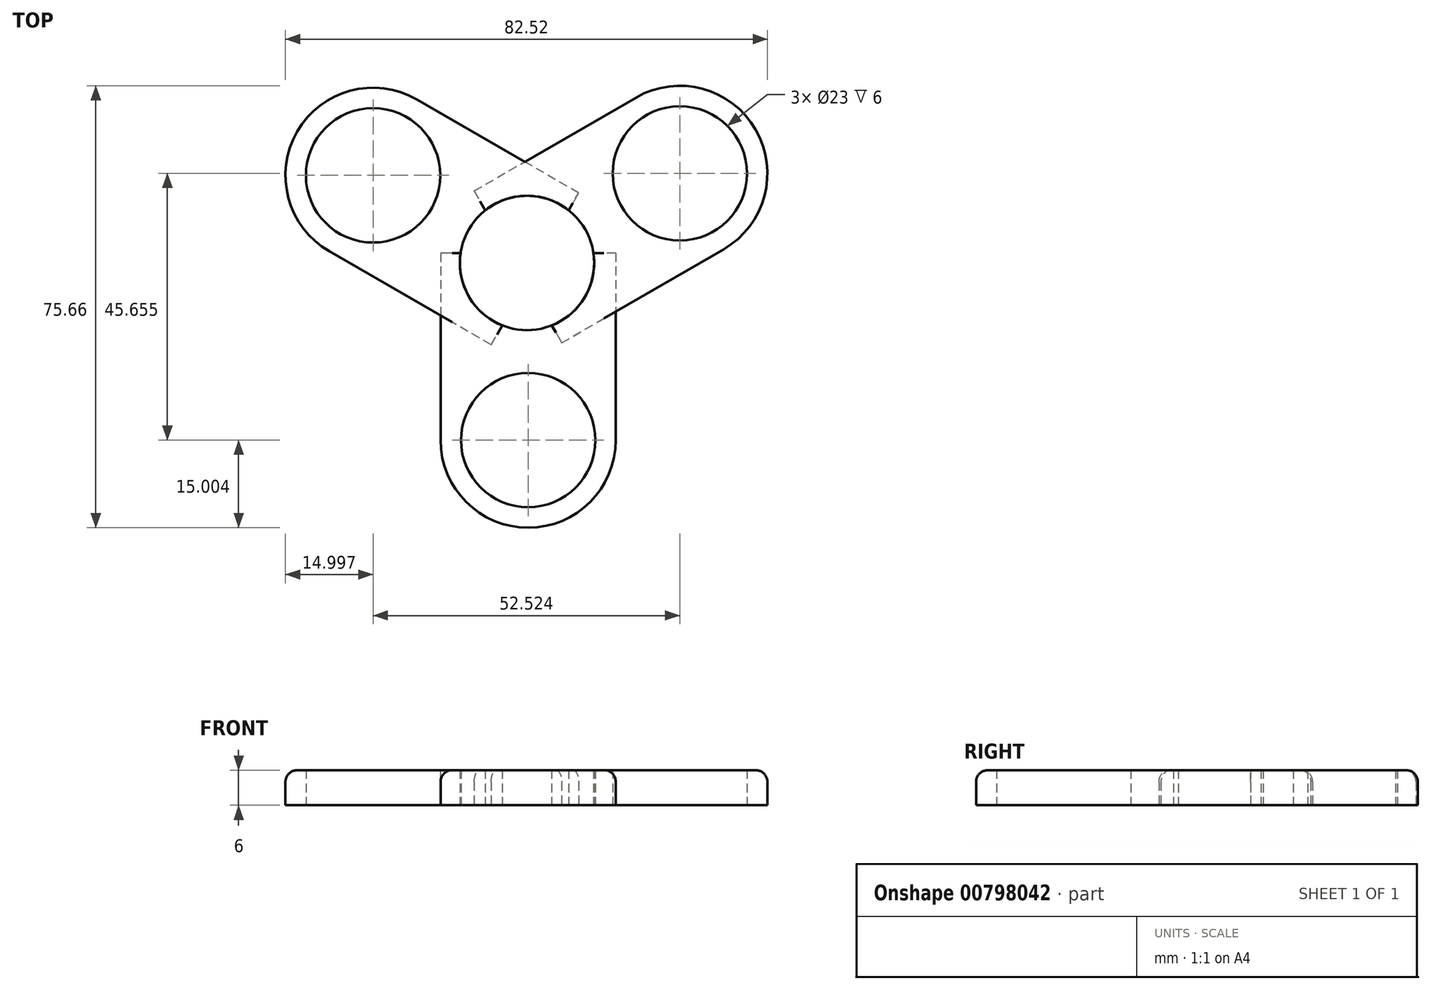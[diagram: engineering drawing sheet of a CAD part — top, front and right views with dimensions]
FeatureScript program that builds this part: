
annotation { "Feature Type Name" : "Feature", "Feature Type Description" : "" }
export const myFeature = defineFeature(function(context is Context, id is Id, definition is map)
    precondition{}
    {
        {
            var Q0;
            Q0=qCreatedBy(makeId("Top.planeOp"),FACE);
            var sketch = newSketch(context, id + "F0", { "sketchPlane" : qUnion([Q0])});
            skLineSegment(sketch, "E0.bottom", {"start": v(15, 0.38) * mm, "end": v(11.18, 0.38) * mm});
            skLineSegment(sketch, "E0.left", {"start": v(15, 0.38) * mm, "end": v(15, -31.62) * mm});
            skLineSegment(sketch, "E0.right", {"start": v(-15, 0.38) * mm, "end": v(-15, -31.62) * mm});
            skArc(sketch, "E1", {"start": v(-15, -31.62) * mm, "mid": v(0, -46.62) * mm, "end": v(15, -31.62) * mm});
            skArc(sketch, "E2", {"start": v(-11.57, 0.38) * mm, "mid": v(-0.2, -12.8) * mm, "end": v(11.18, 0.38) * mm});
            skCircle(sketch, "E3", {"center": v(0, -31.62) * mm, "radius": 11.5 * mm});
            skLineSegment(sketch, "E4.trimOffspring", {"start": v(-11.57, 0.38) * mm, "end": v(-15, 0.38) * mm});
            skSolve(sketch);
        }
        {
            var Q0;
            {var subQ1=sQuery(id+"F0.wireOp",EDGE,"E0.left");Q0=makeQuery(id+"F0.imprint","IMPRINT",FACE,{"disambiguationData":[TD([[makeQuery(id+"F0.imprint","IMPRINT",EDGE,{"derivedFrom":subQ1}),-1.0]])]});}
            extrude(context, id + "F1", {"entities" : qUnion([Q0]), "depth" : 6 * mm, "offsetDistance" : 25 * mm});
        }
        {
            var Q0;
            Q0=makeQuery(id+"F1.opExtrude","SWEPT_BODY",BODY,{"disambiguationData":[OSD([sQuery(id+"F0.wireOp",EDGE,"E0.bottom"),sQuery(id+"F0.wireOp",EDGE,"E0.left"),sQuery(id+"F0.wireOp",EDGE,"E0.right"),sQuery(id+"F0.wireOp",EDGE,"E1"),sQuery(id+"F0.wireOp",EDGE,"E2"),sQuery(id+"F0.wireOp",EDGE,"E3"),sQuery(id+"F0.wireOp",EDGE,"E4.trimOffspring")])]});
            var Q1;
            Q1=makeQuery(id+"F1.opExtrude","SWEPT_FACE",FACE,{"disambiguationData":[OSD([sQuery(id+"F0.wireOp",EDGE,"E2")])]});
            circularPattern(context, id + "F2", {"entities" : qUnion([Q0]), "axis" : qUnion([Q1]), "angle" : 360 * degree, "instanceCount" : 3, "equalSpace" : true});
        }
        {
            var Q0;
            Q0=makeQuery(id+"F2.opPattern","COPY",EDGE,{"derivedFrom":makeQuery(id+"F1.opExtrude","CAP_EDGE",EDGE,{"disambiguationData":[OSD([sQuery(id+"F0.wireOp",EDGE,"E0.left")])],"isStart":false}),"instanceName":"2"});
            var Q1;
            Q1=makeQuery(id+"F2.opPattern","COPY",EDGE,{"derivedFrom":makeQuery(id+"F1.opExtrude","CAP_EDGE",EDGE,{"disambiguationData":[OSD([sQuery(id+"F0.wireOp",EDGE,"E0.left")])],"isStart":false}),"instanceName":"1"});
            var Q2;
            Q2=makeQuery(id+"F1.opExtrude","CAP_EDGE",EDGE,{"disambiguationData":[OSD([sQuery(id+"F0.wireOp",EDGE,"E0.left")])],"isStart":false});
            fillet(context, id + "F3", {"entities" : qUnion([Q0, Q1, Q2]), "radius" : 2 * mm, "tangentPropagation" : true, "allowEdgeOverflow" : false});
        }
    });
